# Revit family: Table-Allermuir-Pause-Coffee_Table-Rectangular-PST156
name_source: partatom
category: Furniture
revit_build: Autodesk Revit Architecture 2012 (Build: 20110309_2315(x64)
units: mm (PartAtom-declared; Revit-internal decimal feet)

## types (1)
- PST156
    04 CSI = 12 51 00
    95 CSI = 12510
    Assembly Code = E2020200
    CAD Blocks URL = http://www.allermuir.net
    Color Availability = See price list for material options
    Fabric Spec Sheets = http://www.allermuir.net
    LEED Stats URL = http://www.allermuir.net
    Leg Base = Plastic - Allermuir - Black
    Legs = Metal - Allermuir - Silver
    Manufacturer = Allermuir
    Manufacturer Fax = (419) 887 5805
    Model = PST156
    Overall Depth = 23.6 "
    Overall Height = 12.8 "
    Overall Width = 59.1 "
    Plastic Arms in Black = No
    Plugin Data URL = http://products.ecoscorecard.com
    Pricing URL = http://www.allermuir.net
    Product Line = Pause Tables
    Product Page URL = http://www.allermuir.net
    Specifications URL = http://www.allermuir.net
    Stacks = No
    Subcategory = Tables
    Table Top = Laminate - Allermuir - White
    URL = http://www.allermuir.net
    Upholstered Back = No
    Upholstered Seat = No
    Weight = 0.0 lb
    ecoScorecard Product Page = http://products.ecoscorecard.com
    ecoScorecard_data = http://thesenatorgroup.ecoscorecard.com

## geometry (parser evidence)
native form markers: Blend x12, Sweep x4
no freeform markers — native parametric forms only
